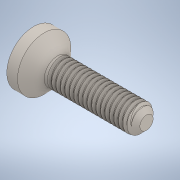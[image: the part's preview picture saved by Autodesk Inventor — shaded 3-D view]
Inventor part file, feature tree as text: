
AUTODESK INVENTOR PART (.ipt)
format: ipt  version: 2020 (Build 240168000, 168)  size: 566,272 bytes
history: native  units: mm
features: other x1, thread x1
ambient origin geometry x8: Origin, YZ Plane, XZ Plane, XY Plane, X Axis, Y Axis, Z Axis, Center Point
bodies: Body1 (feature_tree)
feature tree (2):
  other  "Твердое тело1"
  thread  "Thread1"  [1 undecoded]
note: 1 required parameter value undecoded (feature->parameter linkage not recoverable at this tier; creation-order binding heuristic only, values carry confidence <= 0.55)
